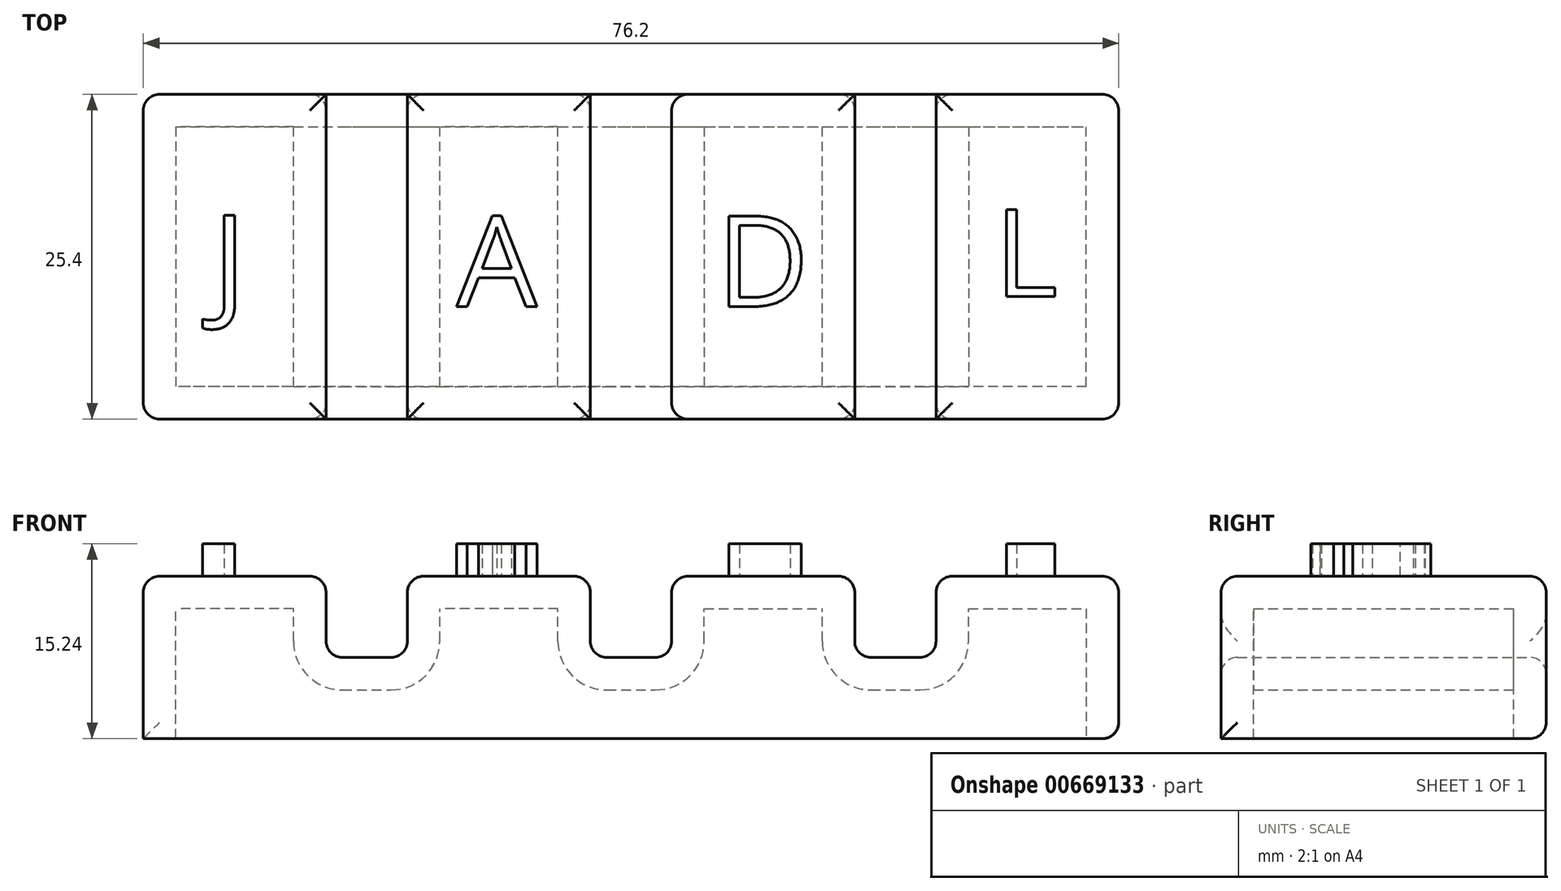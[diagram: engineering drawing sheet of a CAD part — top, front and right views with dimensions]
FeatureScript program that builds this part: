
annotation { "Feature Type Name" : "Feature", "Feature Type Description" : "" }
export const myFeature = defineFeature(function(context is Context, id is Id, definition is map)
    precondition{}
    {
        {
            var Q0;
            Q0=qCreatedBy(makeId("Top.planeOp"),FACE);
            var sketch = newSketch(context, id + "F0", { "sketchPlane" : qUnion([Q0])});
            skLineSegment(sketch, "E0.bottom", {"start": v(38.1, 12.7) * mm, "end": v(-38.1, 12.7) * mm});
            skLineSegment(sketch, "E0.top", {"start": v(38.1, -12.7) * mm, "end": v(-38.1, -12.7) * mm});
            skLineSegment(sketch, "E0.left", {"start": v(38.1, 12.7) * mm, "end": v(38.1, -12.7) * mm});
            skLineSegment(sketch, "E0.right", {"start": v(-38.1, 12.7) * mm, "end": v(-38.1, -12.7) * mm});
            skPoint(sketch, "E0.middle", {"position": v(0, 0) * mm});
            skPoint(sketch, "E1.middle", {"position": v(38.1, 12.7) * mm});
            skSolve(sketch);
        }
        {
            var Q0;
            Q0 = qSketchRegion(id + "F0", true);
            extrude(context, id + "F1", {"entities" : qUnion([Q0]), "depth" : 12.7 * mm, "offsetDistance" : 25.4 * mm});
        }
        {
            var Q0;
            Q0=makeQuery(id+"F1.opExtrude","SWEPT_FACE",FACE,{"disambiguationData":[OSD([sQuery(id+"F0.wireOp",EDGE,"E0.bottom")])]});
            var sketch = newSketch(context, id + "F2", { "sketchPlane" : qUnion([Q0])});
            skLineSegment(sketch, "E2", {"start": v(40.61, 6.35) * mm, "end": v(-38.1, 6.35) * mm, "construction": true});
            skPoint(sketch, "E2.startSnap0", {"position": v(38.1, 6.35) * mm});
            skLineSegment(sketch, "E3.bottom", {"start": v(3.17, 6.35) * mm, "end": v(-3.18, 6.35) * mm});
            skLineSegment(sketch, "E3.top", {"start": v(3.17, 19.05) * mm, "end": v(-3.18, 19.05) * mm});
            skLineSegment(sketch, "E3.left", {"start": v(3.17, 6.35) * mm, "end": v(3.17, 19.05) * mm});
            skLineSegment(sketch, "E3.right", {"start": v(-3.18, 6.35) * mm, "end": v(-3.18, 19.05) * mm});
            skPoint(sketch, "E3.middle", {"position": v(0, 12.7) * mm});
            skLineSegment(sketch, "E4.bottom", {"start": v(23.83, 6.35) * mm, "end": v(17.48, 6.35) * mm});
            skLineSegment(sketch, "E4.top", {"start": v(23.83, 19.05) * mm, "end": v(17.48, 19.05) * mm});
            skLineSegment(sketch, "E4.left", {"start": v(23.83, 6.35) * mm, "end": v(23.83, 19.05) * mm});
            skLineSegment(sketch, "E4.right", {"start": v(17.48, 6.35) * mm, "end": v(17.48, 19.05) * mm});
            skPoint(sketch, "E4.middle", {"position": v(20.65, 12.7) * mm});
            skLineSegment(sketch, "E5.bottom", {"start": v(-23.83, 6.35) * mm, "end": v(-17.48, 6.35) * mm});
            skLineSegment(sketch, "E5.top", {"start": v(-23.83, 19.05) * mm, "end": v(-17.48, 19.05) * mm});
            skLineSegment(sketch, "E5.left", {"start": v(-23.83, 6.35) * mm, "end": v(-23.83, 19.05) * mm});
            skLineSegment(sketch, "E5.right", {"start": v(-17.48, 6.35) * mm, "end": v(-17.48, 19.05) * mm});
            skPoint(sketch, "E5.middle", {"position": v(-20.65, 12.7) * mm});
            skSolve(sketch);
        }
        {
            var Q0;
            Q0 = qSketchRegion(id + "F2", true);
            extrude(context, id + "F3", {"entities" : qUnion([Q0]), "operationType" : NewBodyOperationType.REMOVE, "endBound" : BoundingType.THROUGH_ALL, "oppositeDirection" : true, "depth" : 25.4 * mm, "offsetDistance" : 25.4 * mm});
        }
        {
            var Q0;
            {var subQ0=sQuery(id+"F0.wireOp",EDGE,"E0.bottom");var subQ1=sQuery(id+"F0.wireOp",EDGE,"E0.top");var subQ2=sQuery(id+"F0.wireOp",EDGE,"E0.left");Q0=makeQuery(id+"F3.boolean.opBoolean","SPLIT",FACE,{"disambiguationData":[TD([makeQuery(id+"F1.opExtrude","SWEPT_FACE",FACE,{"disambiguationData":[OSD([subQ2])]})])],"derivedFrom":makeQuery(id+"F1.opExtrude","CAP_FACE",FACE,{"disambiguationData":[OSD([subQ0,subQ1,subQ2,sQuery(id+"F0.wireOp",EDGE,"E0.right")])],"isStart":false})});}
            var Q1;
            {var subQ0=sQuery(id+"F0.wireOp",EDGE,"E0.bottom");var subQ1=sQuery(id+"F0.wireOp",EDGE,"E0.top");Q1=makeQuery(id+"F3.boolean.opBoolean","SPLIT",FACE,{"disambiguationData":[TD([makeQuery(id+"F3.opExtrude","SWEPT_FACE",FACE,{"disambiguationData":[OSD([sQuery(id+"F2.wireOp",EDGE,"E3.right")])]})])],"derivedFrom":makeQuery(id+"F1.opExtrude","CAP_FACE",FACE,{"disambiguationData":[OSD([subQ0,subQ1,sQuery(id+"F0.wireOp",EDGE,"E0.left"),sQuery(id+"F0.wireOp",EDGE,"E0.right")])],"isStart":false})});}
            var Q2;
            {var subQ0=sQuery(id+"F0.wireOp",EDGE,"E0.bottom");Q2=makeQuery(id+"F3.boolean.opBoolean","SPLIT",EDGE,{"disambiguationData":[TD([makeQuery(id+"F3.opExtrude","SWEPT_FACE",FACE,{"disambiguationData":[OSD([sQuery(id+"F2.wireOp",EDGE,"E3.left")])]})])],"derivedFrom":makeQuery(id+"F1.opExtrude","CAP_EDGE",EDGE,{"disambiguationData":[OSD([subQ0])],"isStart":false})});}
            var Q3;
            {var subQ0=sQuery(id+"F0.wireOp",EDGE,"E0.bottom");var subQ1=sQuery(id+"F0.wireOp",EDGE,"E0.right");var subQ2=sQuery(id+"F0.wireOp",EDGE,"E0.top");Q3=makeQuery(id+"F3.boolean.opBoolean","SPLIT",FACE,{"disambiguationData":[TD([makeQuery(id+"F1.opExtrude","SWEPT_FACE",FACE,{"disambiguationData":[OSD([subQ1])]})])],"derivedFrom":makeQuery(id+"F1.opExtrude","CAP_FACE",FACE,{"disambiguationData":[OSD([subQ0,subQ2,sQuery(id+"F0.wireOp",EDGE,"E0.left"),subQ1])],"isStart":false})});}
            var Q4;
            {var subQ0=sQuery(id+"F0.wireOp",EDGE,"E0.bottom");var subQ1=sQuery(id+"F0.wireOp",EDGE,"E0.top");Q4=makeQuery(id+"F3.boolean.opBoolean","SPLIT",FACE,{"disambiguationData":[TD([makeQuery(id+"F3.opExtrude","SWEPT_FACE",FACE,{"disambiguationData":[OSD([sQuery(id+"F2.wireOp",EDGE,"E3.left")])]})])],"derivedFrom":makeQuery(id+"F1.opExtrude","CAP_FACE",FACE,{"disambiguationData":[OSD([subQ0,subQ1,sQuery(id+"F0.wireOp",EDGE,"E0.left"),sQuery(id+"F0.wireOp",EDGE,"E0.right")])],"isStart":false})});}
            var Q5;
            Q5=makeQuery(id+"F3.boolean.opBoolean","COPY",FACE,{"derivedFrom":makeQuery(id+"F3.opExtrude","SWEPT_FACE",FACE,{"disambiguationData":[OSD([sQuery(id+"F2.wireOp",EDGE,"E5.bottom")])]})});
            var Q6;
            Q6=makeQuery(id+"F3.boolean.opBoolean","COPY",FACE,{"derivedFrom":makeQuery(id+"F3.opExtrude","SWEPT_FACE",FACE,{"disambiguationData":[OSD([sQuery(id+"F2.wireOp",EDGE,"E3.right")])]})});
            var Q7;
            Q7=makeQuery(id+"F3.boolean.opBoolean","COPY",EDGE,{"derivedFrom":makeQuery(id+"F3.opExtrude","SWEPT_EDGE",EDGE,{"disambiguationData":[OSD([sQuery(id+"F2.wireOp",EDGE,"E4.bottom"),sQuery(id+"F2.wireOp",EDGE,"E4.right")])]})});
            var Q8;
            Q8=makeQuery(id+"F3.boolean.opBoolean","COPY",FACE,{"derivedFrom":makeQuery(id+"F3.opExtrude","SWEPT_FACE",FACE,{"disambiguationData":[OSD([sQuery(id+"F2.wireOp",EDGE,"E4.bottom")])]})});
            var Q9;
            Q9=makeQuery(id+"F3.boolean.opBoolean","COPY",FACE,{"derivedFrom":makeQuery(id+"F3.opExtrude","SWEPT_FACE",FACE,{"disambiguationData":[OSD([sQuery(id+"F2.wireOp",EDGE,"E3.bottom")])]})});
            var Q10;
            Q10=makeQuery(id+"F1.opExtrude","SWEPT_EDGE",EDGE,{"disambiguationData":[OSD([sQuery(id+"F0.wireOp",EDGE,"E0.top"),sQuery(id+"F0.wireOp",EDGE,"E0.left")])]});
            var Q11;
            Q11=makeQuery(id+"F1.opExtrude","CAP_EDGE",EDGE,{"disambiguationData":[OSD([sQuery(id+"F0.wireOp",EDGE,"E0.left")])],"isStart":true});
            fillet(context, id + "F4", {"entities" : qUnion([Q0, Q1, Q2, Q3, Q4, Q5, Q6, Q7, Q8, Q9, Q10, Q11]), "radius" : 1.27 * mm, "tangentPropagation" : true, "allowEdgeOverflow" : false});
        }
        {
            var Q0;
            {var subQ0=sQuery(id+"F0.wireOp",EDGE,"E0.bottom");var subQ1=makeQuery(id+"F1.opExtrude","SWEPT_FACE",FACE,{"disambiguationData":[OSD([subQ0])]});var subQ2=sQuery(id+"F0.wireOp",EDGE,"E0.left");Q0=makeQuery(id+"F4.opFillet","BLEND_EDGE",EDGE,{"blendedFrom":[makeQuery(id+"F3.boolean.opBoolean","SPLIT",EDGE,{"disambiguationData":[TD([makeQuery(id+"F1.opExtrude","SWEPT_FACE",FACE,{"disambiguationData":[OSD([subQ2])]})])],"derivedFrom":makeQuery(id+"F1.opExtrude","CAP_EDGE",EDGE,{"disambiguationData":[OSD([subQ0])],"isStart":false})}),subQ1],"blendedInto":[subQ1]});}
            var Q1;
            Q1=makeQuery(id+"F1.opExtrude","SWEPT_EDGE",EDGE,{"disambiguationData":[OSD([sQuery(id+"F0.wireOp",EDGE,"E0.bottom"),sQuery(id+"F0.wireOp",EDGE,"E0.right")])]});
            var Q2;
            Q2=makeQuery(id+"F1.opExtrude","SWEPT_EDGE",EDGE,{"disambiguationData":[OSD([sQuery(id+"F0.wireOp",EDGE,"E0.top"),sQuery(id+"F0.wireOp",EDGE,"E0.right")])]});
            var Q3;
            Q3=makeQuery(id+"F1.opExtrude","SWEPT_EDGE",EDGE,{"disambiguationData":[OSD([sQuery(id+"F0.wireOp",EDGE,"E0.bottom"),sQuery(id+"F0.wireOp",EDGE,"E0.left")])]});
            fillet(context, id + "F5", {"entities" : qUnion([Q0, Q1, Q2, Q3]), "radius" : 1.27 * mm, "tangentPropagation" : true, "allowEdgeOverflow" : false});
        }
        {
            var Q0;
            Q0=makeQuery(id+"F1.opExtrude","CAP_FACE",FACE,{"disambiguationData":[OSD([sQuery(id+"F0.wireOp",EDGE,"E0.bottom"),sQuery(id+"F0.wireOp",EDGE,"E0.top"),sQuery(id+"F0.wireOp",EDGE,"E0.left"),sQuery(id+"F0.wireOp",EDGE,"E0.right")])],"isStart":true});
            shell(context, id + "F6", {"entities" : qUnion([Q0]), "thickness" : 2.54 * mm});
        }
        {
            var Q0;
            {var subQ0=sQuery(id+"F0.wireOp",EDGE,"E0.bottom");var subQ1=sQuery(id+"F0.wireOp",EDGE,"E0.right");var subQ2=sQuery(id+"F0.wireOp",EDGE,"E0.top");Q0=makeQuery(id+"F3.boolean.opBoolean","SPLIT",FACE,{"disambiguationData":[TD([makeQuery(id+"F1.opExtrude","SWEPT_FACE",FACE,{"disambiguationData":[OSD([subQ1])]})])],"derivedFrom":makeQuery(id+"F1.opExtrude","CAP_FACE",FACE,{"disambiguationData":[OSD([subQ0,subQ2,sQuery(id+"F0.wireOp",EDGE,"E0.left"),subQ1])],"isStart":false})});}
            var sketch = newSketch(context, id + "F7", { "sketchPlane" : qUnion([Q0])});
            skText(sketch, "E6", { "text": "L", "fontName": "OpenSans-Regular.ttf"});
            const initialGuessF7  = {"E6": [0.0284, -0.00312, 1, 0, 0.00685]};
            skSetInitialGuess(sketch, initialGuessF7);
            skSolve(sketch);
        }
        {
            var Q0;
            Q0 = qSketchRegion(id + "F7", true);
            extrude(context, id + "F8", {"entities" : qUnion([Q0]), "operationType" : NewBodyOperationType.ADD, "depth" : 2.54 * mm, "offsetDistance" : 25.4 * mm});
        }
        {
            var Q0;
            {var subQ0=sQuery(id+"F0.wireOp",EDGE,"E0.bottom");var subQ1=sQuery(id+"F0.wireOp",EDGE,"E0.top");Q0=makeQuery(id+"F3.boolean.opBoolean","SPLIT",FACE,{"disambiguationData":[TD([makeQuery(id+"F3.opExtrude","SWEPT_FACE",FACE,{"disambiguationData":[OSD([sQuery(id+"F2.wireOp",EDGE,"E3.right")])]})])],"derivedFrom":makeQuery(id+"F1.opExtrude","CAP_FACE",FACE,{"disambiguationData":[OSD([subQ0,subQ1,sQuery(id+"F0.wireOp",EDGE,"E0.left"),sQuery(id+"F0.wireOp",EDGE,"E0.right")])],"isStart":false})});}
            var sketch = newSketch(context, id + "F9", { "sketchPlane" : qUnion([Q0])});
            skText(sketch, "E7", { "text": "D", "fontName": "OpenSans-Regular.ttf"});
            skText(sketch, "E8", { "text": "A", "fontName": "OpenSans-Regular.ttf"});
            skText(sketch, "E9", { "text": "J", "fontName": "OpenSans-Regular.ttf"});
            const initialGuessF9  = {"E7": [0.00668, -0.0039, 1, 0, 0.00713], "E8": [-0.01362, -0.0039, 1, 0, 0.00714], "E9": [-0.0327, -0.00384, 1, 0, 0.00713]};
            skSetInitialGuess(sketch, initialGuessF9);
            skSolve(sketch);
        }
        {
            var Q0;
            Q0 = qSketchRegion(id + "F9", true);
            extrude(context, id + "F10", {"entities" : qUnion([Q0]), "operationType" : NewBodyOperationType.ADD, "depth" : 2.54 * mm, "offsetDistance" : 25.4 * mm});
        }
    });
